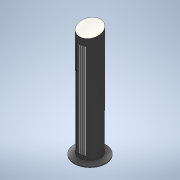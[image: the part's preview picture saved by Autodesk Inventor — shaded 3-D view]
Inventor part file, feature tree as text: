
AUTODESK INVENTOR PART (.ipt)
format: ipt  version: 2022 (Build 260153000, 153)  size: 182,784 bytes
history: native  units: mm
features: sketch x5, plane x3, extrude x3, loft x2, fillet x1, other x1
ambient origin geometry x8: Origin, YZ Plane, XZ Plane, XY Plane, X Axis, Y Axis, Z Axis, Center Point
bodies: Body1 (feature_tree)
feature tree (15):
  sketch  "Sketch1"  dims[d0=30.0mm d1=1.0mm]
  plane  "Work Plane1"
  sketch  "Sketch2"  dims[d2=30.0mm d3=1.0mm]
  plane  "Work Plane2"
  sketch  "Sketch4"  dims[d11=20.0mm d12=0.0mm d13=90.0deg]
  loft  "Loft2"
  loft  "Loft3"
  extrude  "Extrusion1"  TaperAngle=0.0deg  [1 undecoded]
  extrude  "Extrusion2"  TaperAngle=0.0deg  [1 undecoded]
  fillet  "Fillet1"  [1 undecoded]
  plane  "Work Plane3"
  extrude  "Extrusion3"  Depth=5.0mm
  other  "Edges1"
  sketch  "Sketch5"  dims[d14=0.0mm d15=90.0deg d16=0.0mm d17=90.0deg d18=0.0mm d19=90.0deg]
  sketch  "Sketch6"  dims[d20=100.0mm d21=0.0mm d22=5.0mm d23=0.5mm d24=20.0mm d25=0.0mm d26=10.0mm d27=-10.0mm d28=90.0mm d29=10.0mm d30=10.0mm d31=5.0mm d32=5.0mm d33=0.0mm d34=1.0mm d35=0.5mm d36=1.0mm d37=0.5mm d38=1.0mm d39=0.5mm d40=1.0mm d41=0.5mm d42=1.0mm d43=0.5mm d44=1.0mm d45=1.0mm d46=0.5mm]
note: 3 required parameter values undecoded (feature->parameter linkage not recoverable at this tier; creation-order binding heuristic only, values carry confidence <= 0.55)
